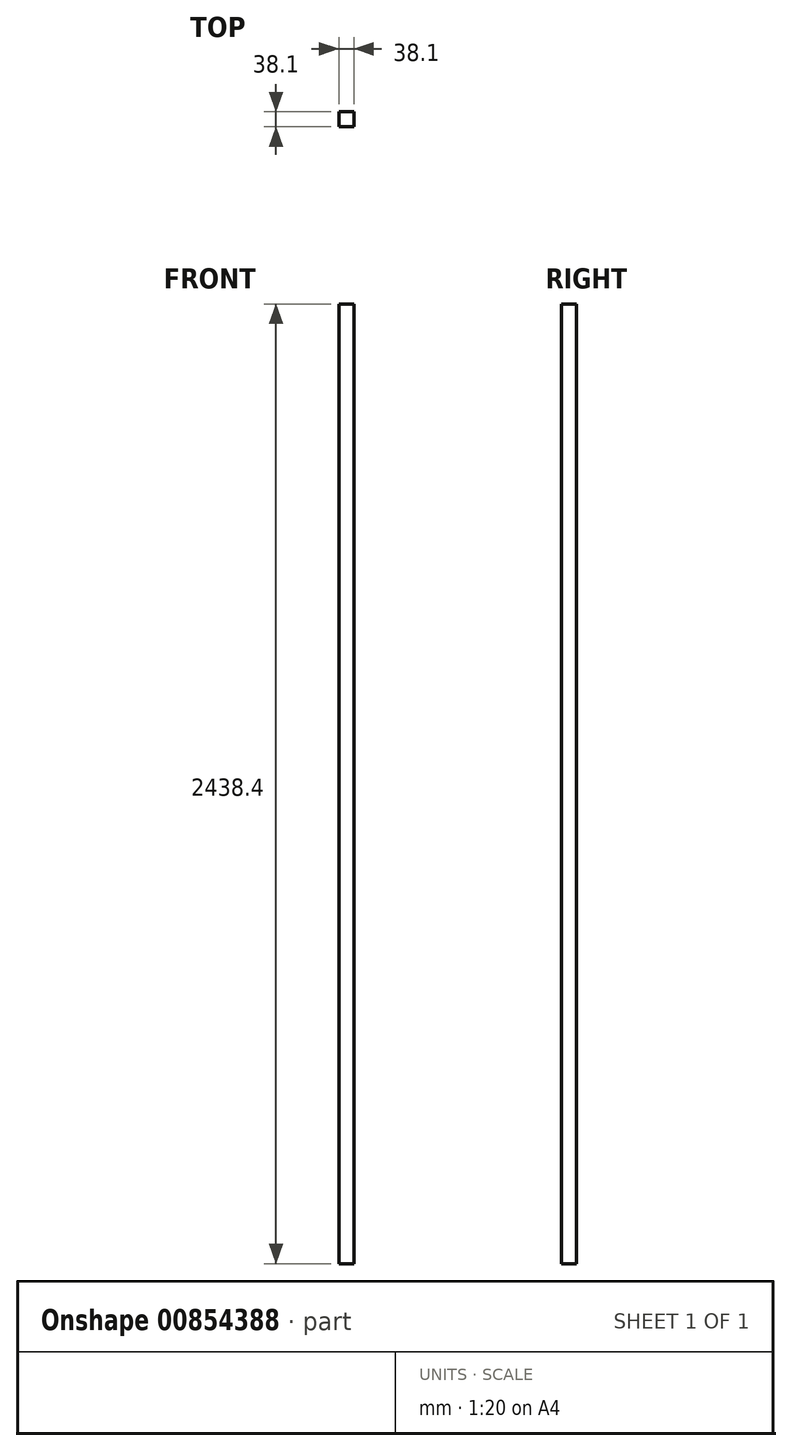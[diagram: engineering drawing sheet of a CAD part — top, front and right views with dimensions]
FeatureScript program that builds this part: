
annotation { "Feature Type Name" : "Feature", "Feature Type Description" : "" }
export const myFeature = defineFeature(function(context is Context, id is Id, definition is map)
    precondition{}
    {
        {
            var Q0;
            Q0=qCreatedBy(makeId("Top.planeOp"),FACE);
            var sketch = newSketch(context, id + "F0", { "sketchPlane" : qUnion([Q0])});
            skLineSegment(sketch, "E0.bottom", {"start": v(19.05, -19.05) * mm, "end": v(-19.05, -19.05) * mm});
            skLineSegment(sketch, "E0.top", {"start": v(19.05, 19.05) * mm, "end": v(-19.05, 19.05) * mm});
            skLineSegment(sketch, "E0.left", {"start": v(19.05, -19.05) * mm, "end": v(19.05, 19.05) * mm});
            skLineSegment(sketch, "E0.right", {"start": v(-19.05, -19.05) * mm, "end": v(-19.05, 19.05) * mm});
            skSolve(sketch);
        }
        {
            var Q0;
            Q0 = qSketchRegion(id + "F0", true);
            extrude(context, id + "F1", {"entities" : qUnion([Q0]), "depth" : 2438.4 * mm, "offsetDistance" : 25.4 * mm});
        }
    });
